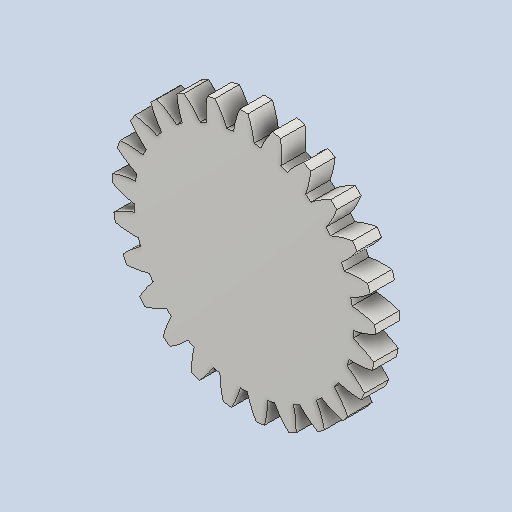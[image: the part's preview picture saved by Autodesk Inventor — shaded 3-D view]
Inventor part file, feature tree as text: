
AUTODESK INVENTOR PART (.ipt)
format: ipt  version: 2024 (Build 280153000, 153)  size: 245,760 bytes
history: native  units: mm (DEFAULTED — no unit token found)
features: plane x3, other x3, extrude x1, sketch x1
ambient origin geometry x8: Origin, YZ Plane, XZ Plane, XY Plane, X Axis, Y Axis, Z Axis, Center Point
bodies: Solid1 (feature_tree)
feature tree (8):
  extrude  "Extrusion1"  Depth=5.0mm TaperAngle=0.0deg
  plane  "Work Plane2"
  plane  "Work Plane8"
  plane  "Work Plane9"
  other  "Spur Gear"
  sketch  "Sketch1"  dims[d0=54.0mm d1=5.0mm d2=0.0mm d3=50.0mm d4=10.0mm d5=0.0mm d16=100.0mm d17=0.0mm d34=1.256637mm d39=0.0mm d41=0.0mm d43=100.0mm d46=100.0mm d47=0.0mm d48=0.0mm]
  other  "Srf1"
  other  "Pitch Diameter"
